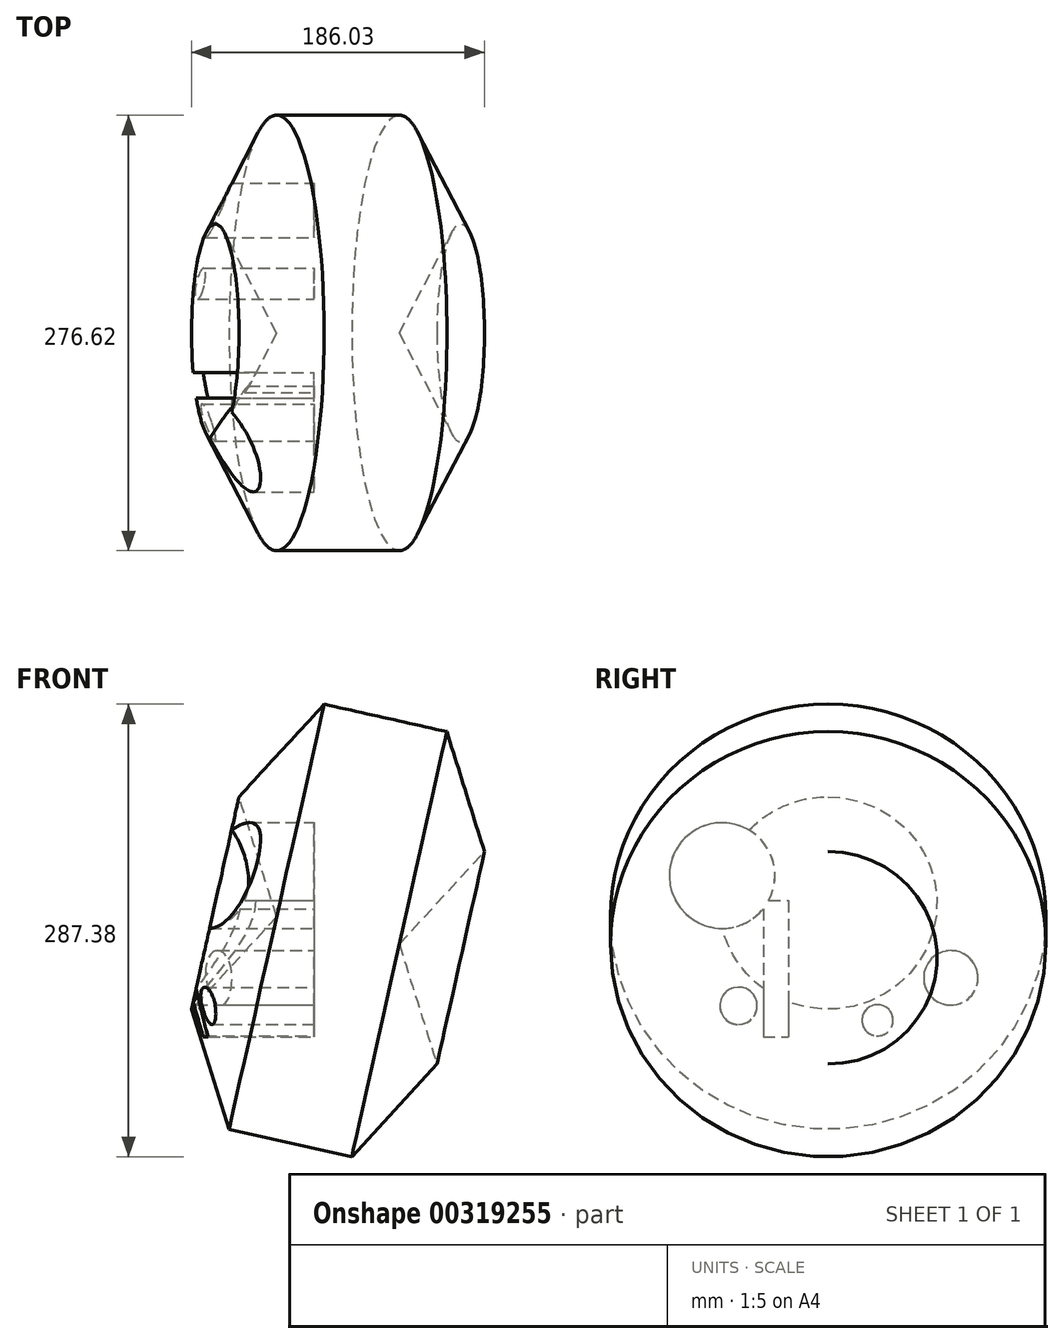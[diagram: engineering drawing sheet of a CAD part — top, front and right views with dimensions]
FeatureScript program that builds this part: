
annotation { "Feature Type Name" : "Feature", "Feature Type Description" : "" }
export const myFeature = defineFeature(function(context is Context, id is Id, definition is map)
    precondition{}
    {
        {
            var Q0;
            Q0=qCreatedBy(makeId("Front.planeOp"),FACE);
            var sketch = newSketch(context, id + "F0", { "sketchPlane" : qUnion([Q0])});
            skCircle(sketch, "E0.cCircle", {"center": v(0, 0) * mm, "radius": 69.16 * mm, "construction": true});
            skLineSegment(sketch, "E0.0", {"start": v(77.93, -17.42) * mm, "end": v(23.88, -76.2) * mm});
            skLineSegment(sketch, "E0.1", {"start": v(23.88, -76.2) * mm, "end": v(-54.05, -58.78) * mm});
            skLineSegment(sketch, "E0.2", {"start": v(-54.05, -58.78) * mm, "end": v(-77.93, 17.42) * mm});
            skLineSegment(sketch, "E0.3", {"start": v(-77.93, 17.42) * mm, "end": v(-23.88, 76.2) * mm});
            skLineSegment(sketch, "E0.4", {"start": v(-23.88, 76.2) * mm, "end": v(54.05, 58.78) * mm});
            skLineSegment(sketch, "E0.5", {"start": v(54.05, 58.78) * mm, "end": v(77.93, -17.42) * mm});
            skPoint(sketch, "E0.0.midPoint", {"position": v(50.9, -46.8) * mm});
            skSolve(sketch);
        }
        {
            var Q0;
            Q0=makeQuery(id+"F0.imprint","IMPRINT",FACE,{"disambiguationData":[TD([[makeQuery(id+"F0.imprint","IMPRINT",EDGE,{"derivedFrom":sQuery(id+"F0.wireOp",EDGE,"E0.0")}),-1.0]])]});
            var Q1;
            Q1=sQuery(id+"F0.wireOp",EDGE,"E0.4");
            revolve(context, id + "F1", {"entities" : qUnion([Q0]), "axis" : qUnion([Q1]), "revolveType" : RevolveType.FULL});
        }
        {
            var Q0;
            Q0=qCreatedBy(makeId("Right.planeOp"),FACE);
            var sketch = newSketch(context, id + "F2", { "sketchPlane" : qUnion([Q0])});
            skCircle(sketch, "E1", {"center": v(77.95, 37.39) * mm, "radius": 17.3 * mm});
            skCircle(sketch, "E2", {"center": v(31.36, 10.4) * mm, "radius": 9.89 * mm});
            skCircle(sketch, "E3", {"center": v(-56.93, 19.6) * mm, "radius": 11.84 * mm});
            skCircle(sketch, "E4", {"center": v(-67.35, 102.37) * mm, "radius": 33.56 * mm});
            skSolve(sketch);
        }
        {
            var Q0;
            Q0 = qSketchRegion(id + "F2", true);
            extrude(context, id + "F3", {"entities" : qUnion([Q0]), "operationType" : NewBodyOperationType.REMOVE, "endBound" : BoundingType.THROUGH_ALL, "oppositeDirection" : true, "depth" : 25.4 * mm});
        }
        {
            var Q0;
            Q0=qCreatedBy(makeId("Right.planeOp"),FACE);
            var sketch = newSketch(context, id + "F4", { "sketchPlane" : qUnion([Q0])});
            skLineSegment(sketch, "E5.bottom", {"start": v(-41.22, 86.45) * mm, "end": v(-25.28, 86.45) * mm});
            skLineSegment(sketch, "E5.top", {"start": v(-41.22, 0) * mm, "end": v(-25.28, 0) * mm});
            skLineSegment(sketch, "E5.left", {"start": v(-41.22, 86.45) * mm, "end": v(-41.22, 0) * mm});
            skLineSegment(sketch, "E5.right", {"start": v(-25.28, 86.45) * mm, "end": v(-25.28, 0) * mm});
            skSolve(sketch);
        }
        {
            var Q0;
            Q0 = qSketchRegion(id + "F4", true);
            extrude(context, id + "F5", {"entities" : qUnion([Q0]), "operationType" : NewBodyOperationType.REMOVE, "endBound" : BoundingType.THROUGH_ALL, "oppositeDirection" : true, "depth" : 25.4 * mm});
        }
    });
